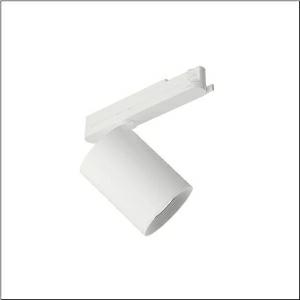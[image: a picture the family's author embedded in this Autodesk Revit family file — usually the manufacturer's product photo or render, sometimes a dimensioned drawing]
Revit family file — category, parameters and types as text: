
# Revit family: spot_21_51se13dbd5b
name_source: partatom
category: Lighting Fixtures
units: mm (PartAtom-declared; Revit-internal decimal feet)

## family parameters
Cut with Voids When Loaded = No
Host = Face
Light Source = No
Part Type = Normal
Room Calculation Point = No
Round Connector Dimension = Use Diameter
Shared = No

## types (1)
- --- (1 x LED, 5410 lm, 42.1 W, 4000K)
    Apparent Load = 42 VA
    CIE Flux Codes = 95 98 99 100 100
    Color Rendering = 90
    Color Temperature = 4000K
    Default Elevation = 1800 mm
    Description = Spot 21, directional spotlight, light control with lens, of PMMA, LED rated luminous flux: 5.200lm, light colour: 940, control gear: ECG Multilumen, with 3-phase adapter, mains connection: 220..240V, AC, 50/60Hz, of aluminium, traffic white (RAL 9016), length: 253mm, diameter: 105mm, protection rating (complete): IP20, insulation class (complete): insulation class I (protective earthing), certification: CE, impact resistance: IK02, permissible ambient temperature for indoor applications: -20..+40°C, packaging unit: 1 piece
    Height = 175 mm
    Lamp = 1 x LED
    Lamp Light Flux = 5410 lm
    Lamp Power = 42.1 W
    Lamp count = 1
    Length = 105 mm
    Luminous efficacy = 129 lm/W
    Manufacturer = Siteco
    ModVariant = No
    Model = 51SE13DBD5B
    Mounting Place = Ceiling
    Mounting Type = Pendant
    Number of Poles = 1
    OnlyDefault = Yes
    Power Factor = 1
    Product Name = Spot 21
    Product group = directional spotlight
    ProductGroupID = 904
    Protection Class = Protection class I
    Protection Degree = IP 20
    RLX_Detail_Level = 1
    RlxData = <blob elided: 17709 chars, md5=9a2de1cf>
    Socket = socket
    Standby Power = 0 W
    System Light Flux = 5410 lm
    System Power = 42 W
    Type Comments = factory setting: luminous flux: 100 % | (ON | ON | ON | ON) | 1050 mA
    Type Image = l_1003976.jpg
    URL = http://relux.com
    VarID = @adj_053277
    Voltage = 0 V
    Weight = 0.00 kg
    Width = 0 mm  [stored 0 ft]

note: [stored X ft] marks values corroborated as IEEE doubles in the binary element streams (Revit-internal decimal feet)

## geometry (parser evidence)
native form markers: Blend x4, Sweep x10
no freeform markers — native parametric forms only
